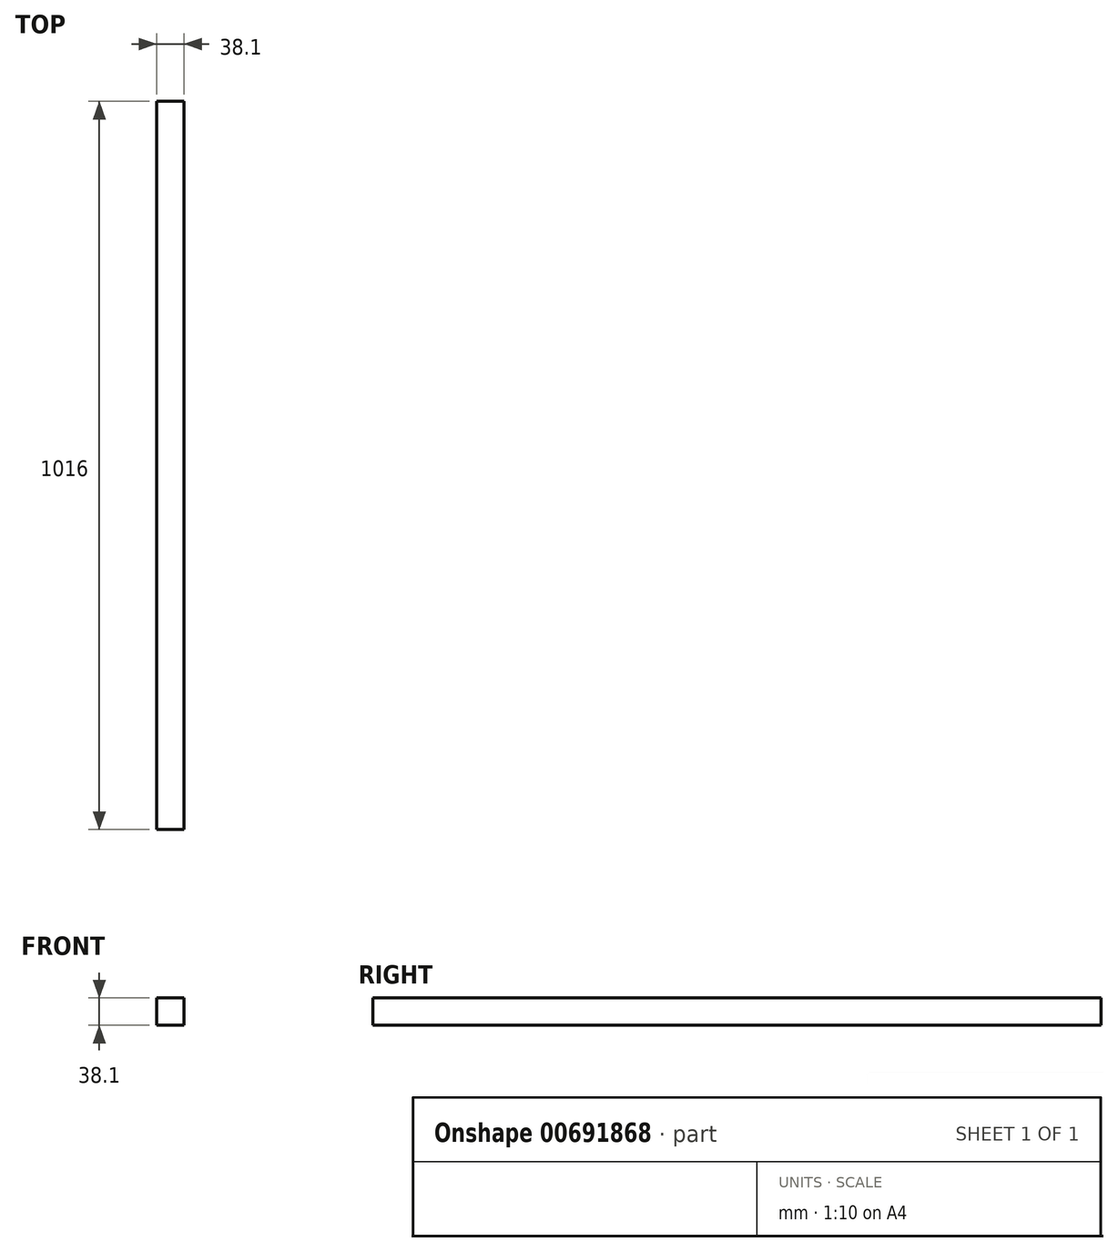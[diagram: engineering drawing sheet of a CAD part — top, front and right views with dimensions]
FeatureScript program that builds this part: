
annotation { "Feature Type Name" : "Feature", "Feature Type Description" : "" }
export const myFeature = defineFeature(function(context is Context, id is Id, definition is map)
    precondition{}
    {
        {
            var Q0;
            Q0=qCreatedBy(makeId("Front.planeOp"),FACE);
            var sketch = newSketch(context, id + "F0", { "sketchPlane" : qUnion([Q0])});
            skLineSegment(sketch, "E0.bottom", {"start": v(0, 0) * mm, "end": v(38.1, 0) * mm});
            skLineSegment(sketch, "E0.top", {"start": v(0, 38.1) * mm, "end": v(38.1, 38.1) * mm});
            skLineSegment(sketch, "E0.left", {"start": v(0, 0) * mm, "end": v(0, 38.1) * mm});
            skLineSegment(sketch, "E0.right", {"start": v(38.1, 0) * mm, "end": v(38.1, 38.1) * mm});
            skSolve(sketch);
        }
        {
            var Q0;
            Q0 = qSketchRegion(id + "F0", true);
            extrude(context, id + "F1", {"entities" : qUnion([Q0]), "depth" : 1016 * mm, "offsetDistance" : 25.4 * mm});
        }
    });
